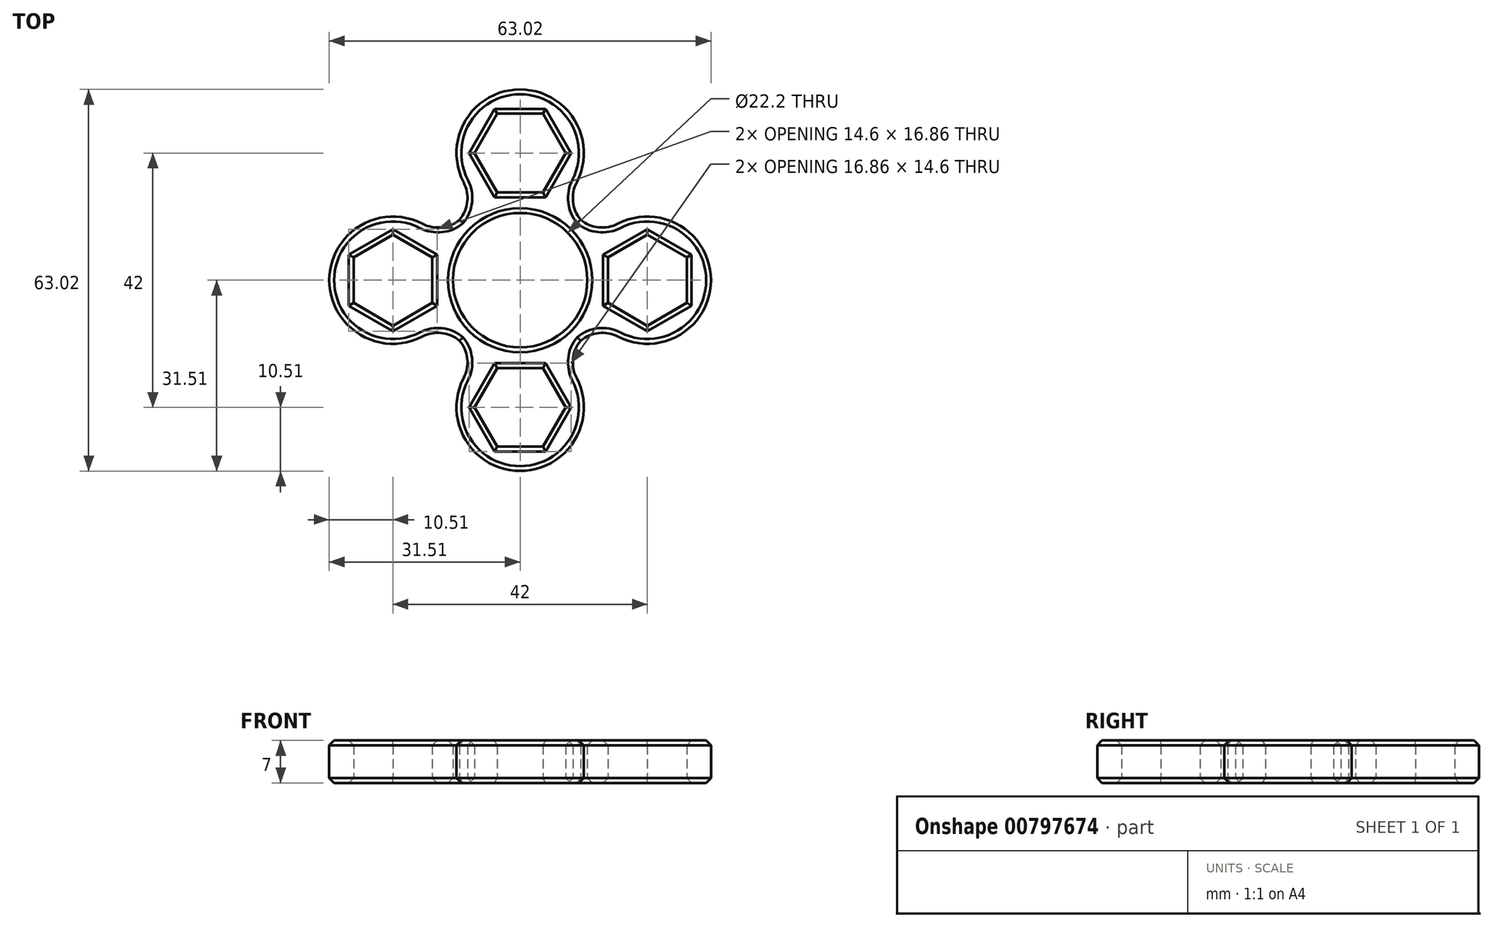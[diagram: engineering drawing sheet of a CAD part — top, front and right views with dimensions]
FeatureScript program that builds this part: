
annotation { "Feature Type Name" : "Feature", "Feature Type Description" : "" }
export const myFeature = defineFeature(function(context is Context, id is Id, definition is map)
    precondition{}
    {
        {
            var Q0;
            Q0=qCreatedBy(makeId("Top.planeOp"),FACE);
            var sketch = newSketch(context, id + "F0", { "sketchPlane" : qUnion([Q0])});
            skCircle(sketch, "E0", {"center": v(0, 0) * mm, "radius": 11.1 * mm});
            skCircle(sketch, "E1.cCircle", {"center": v(0, 0) * mm, "radius": 10.5 * mm, "construction": true});
            skLineSegment(sketch, "E1.0", {"start": v(18.19, -10.5) * mm, "end": v(-18.19, -10.5) * mm, "construction": true});
            skLineSegment(sketch, "E1.1", {"start": v(-18.19, -10.5) * mm, "end": v(0, 21) * mm, "construction": true});
            skLineSegment(sketch, "E1.2", {"start": v(0, 21) * mm, "end": v(18.19, -10.5) * mm, "construction": true});
            skPoint(sketch, "E1.0.midPoint", {"position": v(0, -10.5) * mm});
            skLineSegment(sketch, "E2", {"start": v(0, 0) * mm, "end": v(-9.1, 5.25) * mm});
            skLineSegment(sketch, "E3", {"start": v(-9.1, 5.25) * mm, "end": v(9.1, 5.25) * mm, "construction": true});
            skLineSegment(sketch, "E4", {"start": v(9.1, 5.25) * mm, "end": v(0, 0) * mm});
            skLineSegment(sketch, "E5", {"start": v(0, -10.5) * mm, "end": v(0, 0) * mm, "construction": true});
            skLineSegment(sketch, "E6", {"start": v(9.1, 5.25) * mm, "end": v(0, -10.5) * mm, "construction": true});
            skLineSegment(sketch, "E7", {"start": v(-9.1, 5.25) * mm, "end": v(0, -10.5) * mm, "construction": true});
            skArc(sketch, "E8", {"start": v(9.33, 16.17) * mm, "mid": v(0, 31.5) * mm, "end": v(-9.33, 16.17) * mm});
            skCircle(sketch, "E9.cCircle", {"center": v(0, 21) * mm, "radius": 6.5 * mm, "construction": true});
            skLineSegment(sketch, "E9.0", {"start": v(-3.75, 27.5) * mm, "end": v(3.75, 27.5) * mm});
            skLineSegment(sketch, "E9.1", {"start": v(3.75, 27.5) * mm, "end": v(7.5, 21) * mm});
            skLineSegment(sketch, "E9.2", {"start": v(7.5, 21) * mm, "end": v(3.75, 14.5) * mm});
            skLineSegment(sketch, "E9.3", {"start": v(3.75, 14.5) * mm, "end": v(-3.75, 14.5) * mm});
            skLineSegment(sketch, "E9.4", {"start": v(-3.75, 14.5) * mm, "end": v(-7.5, 21) * mm});
            skLineSegment(sketch, "E9.5", {"start": v(-7.5, 21) * mm, "end": v(-3.75, 27.5) * mm});
            skPoint(sketch, "E9.0.midPoint", {"position": v(0, 27.5) * mm});
            skCircle(sketch, "E10", {"center": v(0, 0) * mm, "radius": 14.1 * mm});
            skArc(sketch, "E11", {"start": v(-10.24, 9.69) * mm, "mid": v(-8.75, 12.78) * mm, "end": v(-9.33, 16.17) * mm});
            skArc(sketch, "E12", {"start": v(9.33, 16.17) * mm, "mid": v(8.75, 12.78) * mm, "end": v(10.24, 9.69) * mm});
            skSolve(sketch);
        }
        {
            var Q0;
            Q0=makeQuery(id+"F0.imprint","IMPRINT",FACE,{"disambiguationData":[TD([[makeQuery(id+"F0.imprint","IMPRINT",EDGE,{"derivedFrom":sQuery(id+"F0.wireOp",EDGE,"E8")}),1.0]])]});
            var Q1;
            Q1=makeQuery(id+"F0.imprint","IMPRINT",FACE,{"disambiguationData":[TD([[makeQuery(id+"F0.imprint","IMPRINT",EDGE,{"derivedFrom":sQuery(id+"F0.wireOp",EDGE,"E0")}),-1.0]])]});
            extrude(context, id + "F1", {"entities" : qUnion([Q0, Q1]), "depth" : 7 * mm, "offsetDistance" : 25 * mm});
        }
        {
            var Q0;
            Q0=makeQuery(id+"F1.opExtrude","SWEPT_BODY",BODY,{"disambiguationData":[OSD([sQuery(id+"F0.wireOp",EDGE,"E0"),sQuery(id+"F0.wireOp",EDGE,"VrMzKTs0-vswA-Jugt-UZDI-ZlNlcJVw19ss"),sQuery(id+"F0.wireOp",EDGE,"E2"),sQuery(id+"F0.wireOp",EDGE,"E4"),sQuery(id+"F0.wireOp",EDGE,"E8"),sQuery(id+"F0.wireOp",EDGE,"FyzykIo4-7ABL-2cN2-SJu5-aql6egmz9Ra5"),sQuery(id+"F0.wireOp",EDGE,"948eeb6a-f036-419e-b3b6-321a4cbb431c0.MirrorCS")])]});
            var Q1;
            Q1=sQuery(id+"F0.wireOp",EDGE,"E0");
            circularPattern(context, id + "F2", {"operationType" : NewBodyOperationType.ADD, "entities" : qUnion([Q0]), "axis" : qUnion([Q1]), "angle" : 360 * degree, "instanceCount" : 4, "equalSpace" : true});
        }
        {
            var Q0;
            {var subQ0=makeQuery(id+"F1.opExtrude","CAP_FACE",FACE,{"disambiguationData":[OSD([sQuery(id+"F0.wireOp",EDGE,"E0"),sQuery(id+"F0.wireOp",EDGE,"E8"),sQuery(id+"F0.wireOp",EDGE,"E9.0"),sQuery(id+"F0.wireOp",EDGE,"E9.1"),sQuery(id+"F0.wireOp",EDGE,"E9.2"),sQuery(id+"F0.wireOp",EDGE,"E9.3"),sQuery(id+"F0.wireOp",EDGE,"E9.4"),sQuery(id+"F0.wireOp",EDGE,"E9.5"),sQuery(id+"F0.wireOp",EDGE,"E10"),sQuery(id+"F0.wireOp",EDGE,"E11"),sQuery(id+"F0.wireOp",EDGE,"E12")])],"isStart":true});Q0=makeQuery(id+"F2.boolean.opBoolean","MERGE",FACE,{"derivedFrom":[subQ0,makeQuery(id+"F2.opPattern","COPY",FACE,{"derivedFrom":subQ0,"instanceName":"1"}),makeQuery(id+"F2.opPattern","COPY",FACE,{"derivedFrom":subQ0,"instanceName":"2"}),makeQuery(id+"F2.opPattern","COPY",FACE,{"derivedFrom":subQ0,"instanceName":"3"})]});}
            var Q1;
            {var subQ0=makeQuery(id+"F1.opExtrude","CAP_FACE",FACE,{"disambiguationData":[OSD([sQuery(id+"F0.wireOp",EDGE,"E0"),sQuery(id+"F0.wireOp",EDGE,"E8"),sQuery(id+"F0.wireOp",EDGE,"E9.0"),sQuery(id+"F0.wireOp",EDGE,"E9.1"),sQuery(id+"F0.wireOp",EDGE,"E9.2"),sQuery(id+"F0.wireOp",EDGE,"E9.3"),sQuery(id+"F0.wireOp",EDGE,"E9.4"),sQuery(id+"F0.wireOp",EDGE,"E9.5"),sQuery(id+"F0.wireOp",EDGE,"E10"),sQuery(id+"F0.wireOp",EDGE,"E11"),sQuery(id+"F0.wireOp",EDGE,"E12")])],"isStart":false});Q1=makeQuery(id+"F2.boolean.opBoolean","MERGE",FACE,{"derivedFrom":[subQ0,makeQuery(id+"F2.opPattern","COPY",FACE,{"derivedFrom":subQ0,"instanceName":"1"}),makeQuery(id+"F2.opPattern","COPY",FACE,{"derivedFrom":subQ0,"instanceName":"2"}),makeQuery(id+"F2.opPattern","COPY",FACE,{"derivedFrom":subQ0,"instanceName":"3"})]});}
            chamfer(context, id + "F3", {"entities" : qUnion([Q0, Q1]), "width" : .8 * mm, "tangentPropagation" : true});
        }
    });
